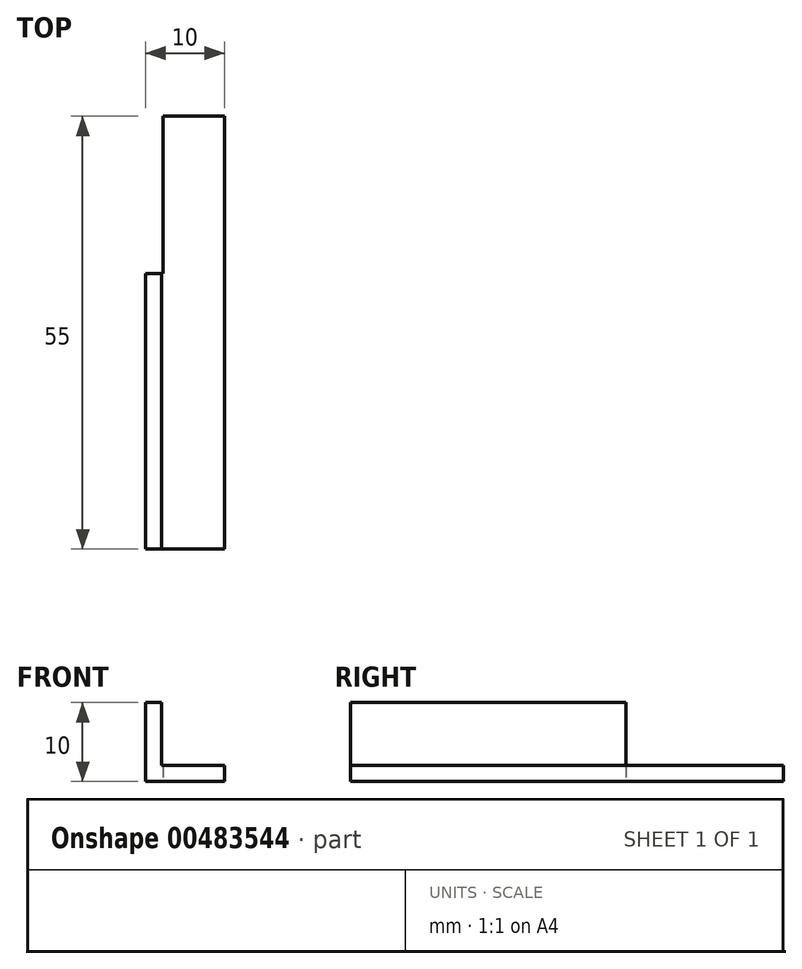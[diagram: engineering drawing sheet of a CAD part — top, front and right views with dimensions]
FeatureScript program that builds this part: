
annotation { "Feature Type Name" : "Feature", "Feature Type Description" : "" }
export const myFeature = defineFeature(function(context is Context, id is Id, definition is map)
    precondition{}
    {
        {
            var Q0;
            Q0=qCreatedBy(makeId("Front.planeOp"),FACE);
            var sketch = newSketch(context, id + "F0", { "sketchPlane" : qUnion([Q0])});
            skLineSegment(sketch, "E0", {"start": v(0, 0) * mm, "end": v(10, 0) * mm});
            skLineSegment(sketch, "E1", {"start": v(10, 0) * mm, "end": v(10, 2) * mm});
            skLineSegment(sketch, "E2", {"start": v(10, 2) * mm, "end": v(2, 2) * mm});
            skLineSegment(sketch, "E3", {"start": v(2, 2) * mm, "end": v(2, 10) * mm});
            skLineSegment(sketch, "E4", {"start": v(2, 10) * mm, "end": v(0, 10) * mm});
            skLineSegment(sketch, "E5", {"start": v(0, 10) * mm, "end": v(0, 0) * mm});
            skSolve(sketch);
        }
        {
            var Q0;
            Q0=qSketchRegion(id+"F0",true);
            extrude(context, id + "F1", {"entities" : qUnion([Q0]), "depth" : 55 * mm, "offsetDistance" : 25 * mm});
        }
        {
            var Q0;
            Q0=makeQuery(id+"F1.opExtrude","SWEPT_FACE",FACE,{"disambiguationData":[OSD([sQuery(id+"F0.wireOp",EDGE,"E5")])]});
            var sketch = newSketch(context, id + "F2", { "sketchPlane" : qUnion([Q0])});
            skLineSegment(sketch, "E6.bottom", {"start": v(0, 10) * mm, "end": v(20, 10) * mm});
            skLineSegment(sketch, "E6.top", {"start": v(0, 0) * mm, "end": v(20, 0) * mm});
            skLineSegment(sketch, "E6.left", {"start": v(0, 10) * mm, "end": v(0, 0) * mm});
            skLineSegment(sketch, "E6.right", {"start": v(20, 10) * mm, "end": v(20, 0) * mm});
            skSolve(sketch);
        }
        {
            var Q0;
            Q0=qSketchRegion(id+"F2",true);
            extrude(context, id + "F3", {"entities" : qUnion([Q0]), "operationType" : NewBodyOperationType.REMOVE, "oppositeDirection" : true, "depth" : 2.2 * mm, "offsetDistance" : 25 * mm});
        }
    });
